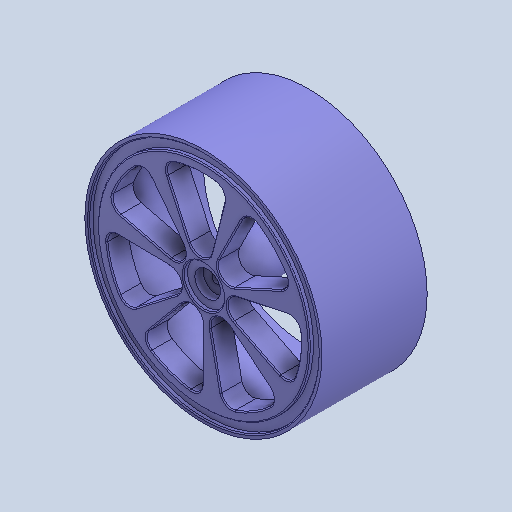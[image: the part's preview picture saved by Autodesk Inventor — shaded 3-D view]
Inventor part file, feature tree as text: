
AUTODESK INVENTOR PART (.ipt)
format: ipt  version: 2024 (Build 280153000, 153)  size: 310,784 bytes
history: native  units: in
note: dims shown in document units (in); Inventor stores cm internally (conversion verified against a paired STEP export)
features: fillet x1
ambient origin geometry x8: Origin, YZ Plane, XZ Plane, XY Plane, X Axis, Y Axis, Z Axis, Center Point
bodies: Solid1 (feature_tree)
feature tree (1):
  fillet  "圆角11"  [1 undecoded]
note: 1 required parameter value undecoded (feature->parameter linkage not recoverable at this tier; creation-order binding heuristic only, values carry confidence <= 0.55)
